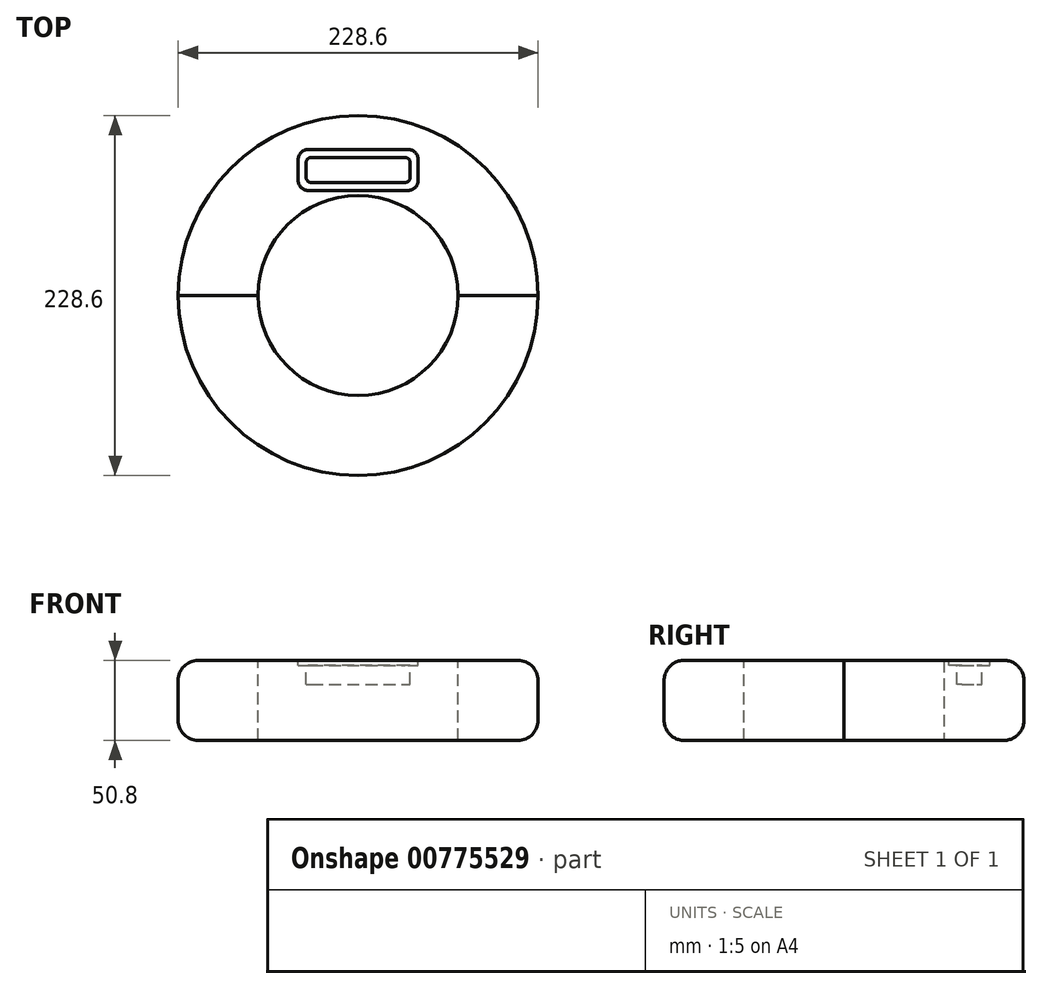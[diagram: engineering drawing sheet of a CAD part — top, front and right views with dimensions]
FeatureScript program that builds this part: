
annotation { "Feature Type Name" : "Feature", "Feature Type Description" : "" }
export const myFeature = defineFeature(function(context is Context, id is Id, definition is map)
    precondition{}
    {
        {
            var Q0;
            Q0=qCreatedBy(makeId("Front.planeOp"),FACE);
            var sketch = newSketch(context, id + "F0", { "sketchPlane" : qUnion([Q0])});
            skLineSegment(sketch, "E0", {"start": v(38.1, 0) * mm, "end": v(0, 0) * mm});
            skLineSegment(sketch, "E1", {"start": v(50.8, 12.7) * mm, "end": v(50.8, 38.1) * mm});
            skLineSegment(sketch, "E2", {"start": v(38.1, 50.8) * mm, "end": v(0, 50.8) * mm});
            skLineSegment(sketch, "E3", {"start": v(0, 0) * mm, "end": v(0, 50.8) * mm});
            skPoint(sketch, "E4.visualSharp", {"position": v(50.8, 0) * mm});
            skArc(sketch, "E4.filletArc", {"start": v(38.1, 0) * mm, "mid": v(47.08, 3.72) * mm, "end": v(50.8, 12.7) * mm});
            skPoint(sketch, "E5.visualSharp", {"position": v(50.8, 50.8) * mm});
            skArc(sketch, "E5.filletArc", {"start": v(50.8, 38.1) * mm, "mid": v(47.08, 47.08) * mm, "end": v(38.1, 50.8) * mm});
            skLineSegment(sketch, "E6", {"start": v(-63.5, 64.91) * mm, "end": v(-63.5, -24.83) * mm, "construction": true});
            skSolve(sketch);
        }
        {
            var Q0;
            Q0=makeQuery(id+"F0.imprint","IMPRINT",FACE,{"disambiguationData":[TD([[makeQuery(id+"F0.imprint","IMPRINT",EDGE,{"derivedFrom":sQuery(id+"F0.wireOp",EDGE,"E0")}),-1.0]])]});
            var Q1;
            Q1=sQuery(id+"F0.wireOp",EDGE,"E6");
            revolve(context, id + "F1", {"surfaceOperationType" : NewSurfaceOperationType.NEW, "entities" : qUnion([Q0]), "axis" : qUnion([Q1]), "revolveType" : RevolveType.ONE_DIRECTION, "angle" : 180 * degree});
        }
        {
            var Q0;
            Q0=makeQuery(id+"F0.imprint","IMPRINT",FACE,{"disambiguationData":[TD([[makeQuery(id+"F0.imprint","IMPRINT",EDGE,{"derivedFrom":sQuery(id+"F0.wireOp",EDGE,"E0")}),-1.0]])]});
            var Q1;
            Q1=sQuery(id+"F0.wireOp",EDGE,"E6");
            revolve(context, id + "F2", {"surfaceOperationType" : NewSurfaceOperationType.NEW, "entities" : qUnion([Q0]), "axis" : qUnion([Q1]), "revolveType" : RevolveType.ONE_DIRECTION, "oppositeDirection" : true, "angle" : 180 * degree});
        }
        {
            var Q0;
            Q0=makeQuery(id+"F2.opRevolve","SWEPT_FACE",FACE,{"disambiguationData":[OSD([sQuery(id+"F0.wireOp",EDGE,"E2")])]});
            var sketch = newSketch(context, id + "F3", { "sketchPlane" : qUnion([Q0])});
            skLineSegment(sketch, "E7", {"start": v(-63.5, 0) * mm, "end": v(-63.5, 112.47) * mm, "construction": true});
            skLineSegment(sketch, "E8", {"start": v(-63.5, 66.67) * mm, "end": v(-95.25, 66.67) * mm});
            skLineSegment(sketch, "E9", {"start": v(-101.6, 73.02) * mm, "end": v(-101.6, 86.36) * mm});
            skLineSegment(sketch, "E10", {"start": v(-95.25, 92.7) * mm, "end": v(-63.5, 92.7) * mm});
            skLineSegment(sketch, "E11.0", {"start": v(-93.34, 87.63) * mm, "end": v(-63.5, 87.63) * mm});
            skLineSegment(sketch, "E11.1", {"start": v(-96.52, 74.93) * mm, "end": v(-96.52, 84.45) * mm});
            skLineSegment(sketch, "E11.2", {"start": v(-63.5, 71.75) * mm, "end": v(-93.34, 71.75) * mm});
            skPoint(sketch, "E12.visualSharp", {"position": v(-101.6, 92.71) * mm});
            skArc(sketch, "E12.filletArc", {"start": v(-95.25, 92.71) * mm, "mid": v(-99.74, 90.85) * mm, "end": v(-101.6, 86.36) * mm});
            skPoint(sketch, "E13.visualSharp", {"position": v(-101.6, 66.67) * mm});
            skArc(sketch, "E13.filletArc", {"start": v(-101.6, 73.02) * mm, "mid": v(-99.74, 68.53) * mm, "end": v(-95.25, 66.67) * mm});
            skPoint(sketch, "E14.visualSharp", {"position": v(-96.52, 71.75) * mm});
            skArc(sketch, "E14.filletArc", {"start": v(-96.52, 74.93) * mm, "mid": v(-95.6, 72.68) * mm, "end": v(-93.34, 71.75) * mm});
            skPoint(sketch, "E15.visualSharp", {"position": v(-96.52, 87.63) * mm});
            skArc(sketch, "E15.filletArc", {"start": v(-93.34, 87.63) * mm, "mid": v(-95.6, 86.7) * mm, "end": v(-96.52, 84.45) * mm});
            skLineSegment(sketch, "E16.MirrorCS", {"start": v(-31.75, 92.7) * mm, "end": v(-63.5, 92.7) * mm});
            skArc(sketch, "E17.MirrorCS", {"start": v(-31.75, 92.71) * mm, "mid": v(-27.26, 90.85) * mm, "end": v(-25.4, 86.36) * mm});
            skLineSegment(sketch, "E18.MirrorCS", {"start": v(-25.4, 73.02) * mm, "end": v(-25.4, 86.36) * mm});
            skLineSegment(sketch, "E19.MirrorCS", {"start": v(-33.66, 87.63) * mm, "end": v(-63.5, 87.63) * mm});
            skArc(sketch, "E20.MirrorCS", {"start": v(-33.66, 87.63) * mm, "mid": v(-31.4, 86.7) * mm, "end": v(-30.48, 84.45) * mm});
            skLineSegment(sketch, "E21.MirrorCS", {"start": v(-30.48, 74.93) * mm, "end": v(-30.48, 84.45) * mm});
            skArc(sketch, "E22.MirrorCS", {"start": v(-30.48, 74.93) * mm, "mid": v(-31.4, 72.68) * mm, "end": v(-33.66, 71.75) * mm});
            skLineSegment(sketch, "E23.MirrorCS", {"start": v(-63.5, 66.67) * mm, "end": v(-31.75, 66.67) * mm});
            skLineSegment(sketch, "E24.MirrorCS", {"start": v(-63.5, 71.75) * mm, "end": v(-33.66, 71.75) * mm});
            skArc(sketch, "E25.MirrorCS", {"start": v(-25.4, 73.02) * mm, "mid": v(-27.26, 68.53) * mm, "end": v(-31.75, 66.67) * mm});
            skSolve(sketch);
        }
        {
            var Q0;
            Q0=makeQuery(id+"F3.imprint","IMPRINT",FACE,{"disambiguationData":[TD([[makeQuery(id+"F3.imprint","IMPRINT",EDGE,{"derivedFrom":sQuery(id+"F3.wireOp",EDGE,"E8")}),-1.0]])]});
            extrude(context, id + "F4", {"entities" : qUnion([Q0]), "operationType" : NewBodyOperationType.REMOVE, "oppositeDirection" : true, "depth" : 3.17 * mm, "offsetDistance" : 25.4 * mm});
        }
        {
            var Q0;
            Q0=makeQuery(id+"F4.boolean.opBoolean","SPLIT",FACE,{"disambiguationData":[TD([makeQuery(id+"F4.opExtrude","SWEPT_FACE",FACE,{"disambiguationData":[OSD([sQuery(id+"F3.wireOp",EDGE,"E11.1")])]})])],"derivedFrom":makeQuery(id+"F2.opRevolve","SWEPT_FACE",FACE,{"disambiguationData":[OSD([sQuery(id+"F0.wireOp",EDGE,"E2")])]})});
            extrude(context, id + "F5", {"entities" : qUnion([Q0]), "operationType" : NewBodyOperationType.REMOVE, "oppositeDirection" : true, "depth" : 15.24 * mm, "offsetDistance" : 25.4 * mm});
        }
    });
